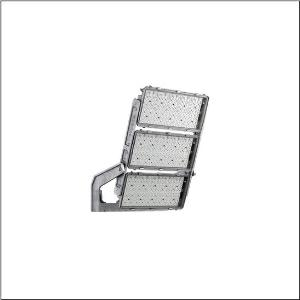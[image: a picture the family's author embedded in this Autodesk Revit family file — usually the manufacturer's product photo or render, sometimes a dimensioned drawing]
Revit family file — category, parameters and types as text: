
# Revit family: floodlight_fl_11_maxi_pro_remote___pl64_5xa779427v01aa_f124
name_source: partatom
category: Lighting Fixtures
units: mm (PartAtom-declared; Revit-internal decimal feet)

## family parameters
Cut with Voids When Loaded = No
Host = Face
Light Source = No
Part Type = Normal
Room Calculation Point = No
Round Connector Dimension = Use Diameter
Shared = No

## types (1)
- --- (1 x LED, 220410 lm, 1540.1 W, 5000K)
    Apparent Load = 1540 VA
    CIE Flux Codes = 28 79 98 100 100
    Color Rendering = 70
    Color Temperature = 5000K
    Default Elevation = 1800 mm
    Description = Floodlight FL 11  maxi  pro Remote floodlight; light control with lens of PMMA; cover panel of toughened safety glass, transparent; light distribution: PL64, asymmetric direct distribution, LEDcolour temperature: 5000K, rated luminous flux: 220.410lm, colour rendering: CRI > 70, light colour: 750; luminous efficacy: 143lm/W; brightness control: DALI 2 (1 DALI address); with terminal, 8-pole, max. 2.5mm², mains connection: 220..240V/380..400V AC, 50/60Hz, surge voltage resistance: line to ground: 10kV, ECG replaceable separately, no afterglow with DALI off / DMX off command, LED unit replaceable without ESD environment, dustproof LED module, dimming range 10..100%; 1540W floodlight with 2x LED unit of diecast aluminium, coated grey; length: 713mm / width: 651mm / height: 338mm; mounting bracket, of diecast aluminium, uncoated, natural, equipment: Power, protection rating (complete): IP66; insulation class (complete): insulation class I (protective earthing); certification: CE, ENEC, VDE; ball protection: ball impact resistance with accessories, impact resistance: IK07; only for outdoor installations, rated ambient temperature 10°C, permissible operating ambient temperature: -40..+30°C, permissible storage temperature: -40..+85°C; packaging unit: 1 piece

Light Distribution: PL64
    Height = 320 mm
    Lamp = 1 x LED
    Lamp Light Flux = 220410 lm
    Lamp Power = 1540.1 W
    Lamp count = 1
    Length = 1002 mm
    Luminous efficacy = 143 lm/W
    Manufacturer = Siteco
    ModVariant = No
    Model = 5XA779427V01AA
    Mounting Place = Ceiling
    Mounting Type = Surface mounted
    Number of Poles = 1
    OnlyDefault = Yes
    Power Factor = 1
    Product Name = Floodlight FL 11 maxi pro Remote | PL64
    Product group = floodlight | ceiling mounted
    ProductGroupID = 302
    Protection Class = Protection class I
    Protection Degree = IP 66
    RLX_Detail_Level = 1
    RLX_Emergency_Light_Flux = 0 lm
    RLX_Emergency_Type = 0
    RLX_Emergency_Type_DB = No
    RlxData = <blob elided: 52325 chars, md5=332f2319>
    Socket = socket
    Standby Power = 0 W
    System Light Flux = 220410 lm
    System Power = 1540 W
    Type Comments = factory setting: luminous flux: 100 % | dim-lin: 254 | 1080 mA
    Type Image = l_1006784.jpg
    URL = http://relux.com
    VarID = @adj_039399
    Voltage = 0 V
    Weight = 0.00 kg
    Width = 655 mm

## geometry (parser evidence)
native form markers: Blend x4, Sweep x15
no freeform markers — native parametric forms only
